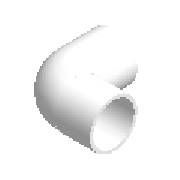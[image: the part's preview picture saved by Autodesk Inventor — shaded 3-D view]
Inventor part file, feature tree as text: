
AUTODESK INVENTOR PART (.ipt)
format: ipt  version: 2023 (Build 270158000, 158)  size: 223,744 bytes
history: native  units: mm (DEFAULTED — no unit token found)
features: other x6, revolve x3, sketch x2, projected_geometry x1
ambient origin geometry x8: Origin, YZ Plane, XZ Plane, XY Plane, X Axis, Y Axis, Z Axis, Center Point
bodies: Solid1 (feature_tree)
feature tree (12):
  sketch  "Sketch1"  dims[d0=86.0mm d1=81.0mm]
  revolve  "Revolution1"  [1 undecoded]
  revolve  "Revolution2"  [1 undecoded]
  revolve  "Revolution3"  [1 undecoded]
  other  "Work Axis1"
  other  "Work Point1"
  other  "Work Point2"
  other  "Work Axis2"
  other  "Work Point3"
  other  "Work Point4"
  sketch  "Sketch2"  dims[d2=160.0mm d3=11.9mm d4=86.0mm d5=11.9mm d6=160.0mm d7=81.0mm d139=90.0deg d140=90.0deg d8=0.01mm d9=183.8mm d10=152.0mm d11=90.0deg]
  projected_geometry  "Projected Loop2"
note: 3 required parameter values undecoded (feature->parameter linkage not recoverable at this tier; creation-order binding heuristic only, values carry confidence <= 0.55)
